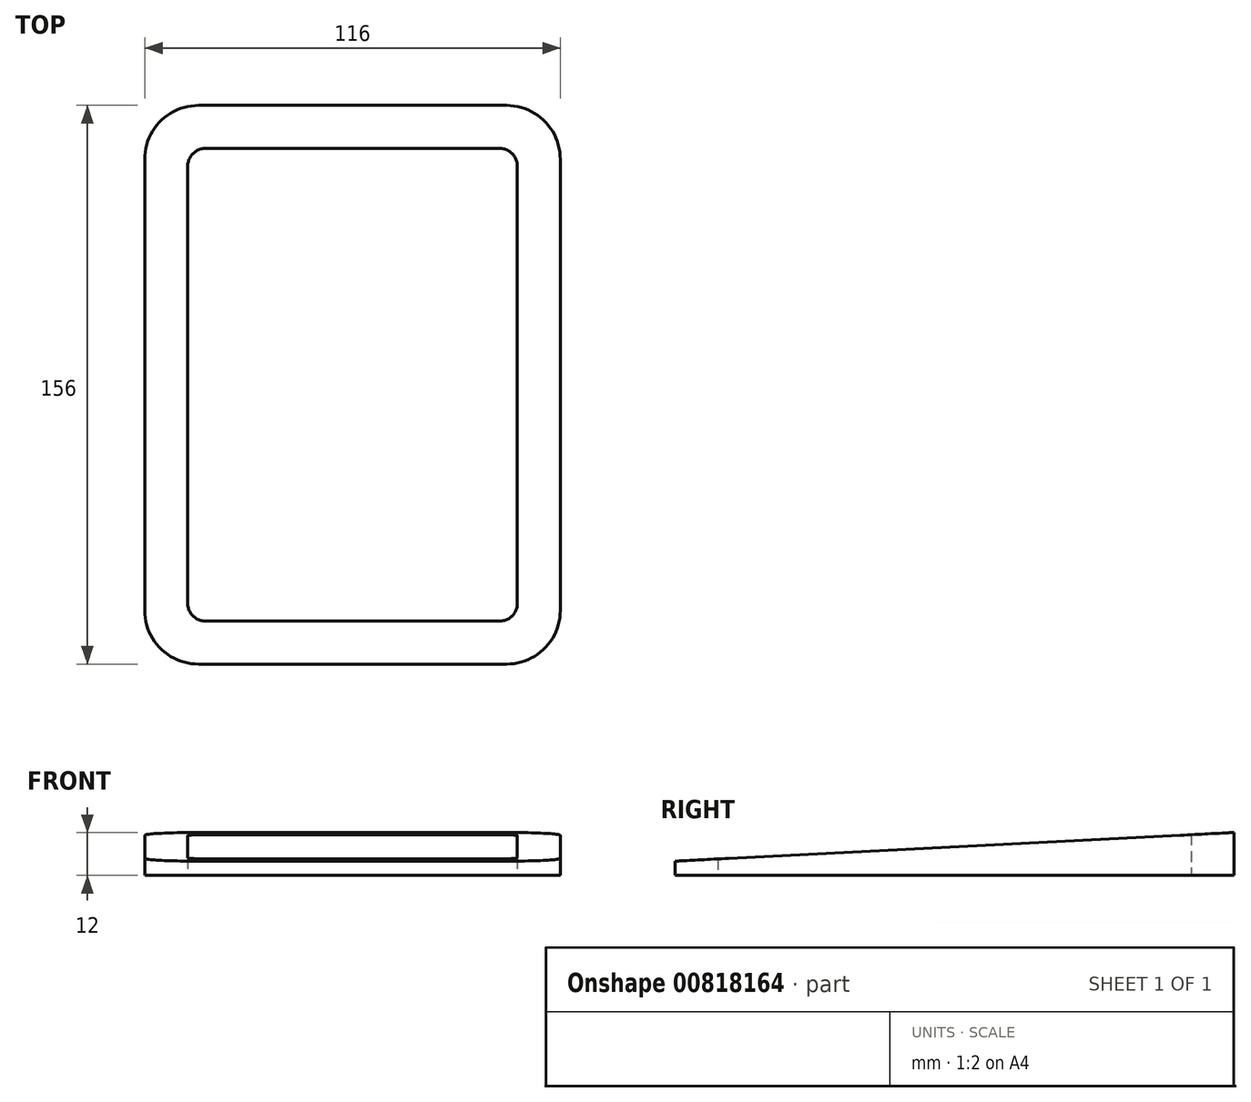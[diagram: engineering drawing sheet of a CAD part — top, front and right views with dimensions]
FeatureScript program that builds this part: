
annotation { "Feature Type Name" : "Feature", "Feature Type Description" : "" }
export const myFeature = defineFeature(function(context is Context, id is Id, definition is map)
    precondition{}
    {
        {
            var Q0;
            Q0=qCreatedBy(makeId("Top.planeOp"),FACE);
            var sketch = newSketch(context, id + "F0", { "sketchPlane" : qUnion([Q0])});
            skLineSegment(sketch, "E0.bottom", {"start": v(-58, 78) * mm, "end": v(58, 78) * mm});
            skLineSegment(sketch, "E0.top", {"start": v(-58, -78) * mm, "end": v(58, -78) * mm});
            skLineSegment(sketch, "E0.left", {"start": v(-58, 78) * mm, "end": v(-58, -78) * mm});
            skLineSegment(sketch, "E0.right", {"start": v(58, 78) * mm, "end": v(58, -78) * mm});
            skLineSegment(sketch, "E1.bottom", {"start": v(-46, 66) * mm, "end": v(46, 66) * mm});
            skLineSegment(sketch, "E1.top", {"start": v(-46, -66) * mm, "end": v(46, -66) * mm});
            skLineSegment(sketch, "E1.left", {"start": v(-46, 66) * mm, "end": v(-46, -66) * mm});
            skLineSegment(sketch, "E1.right", {"start": v(46, 66) * mm, "end": v(46, -66) * mm});
            skSolve(sketch);
        }
        {
            var Q0;
            Q0=makeQuery(id+"F0.imprint","IMPRINT",FACE,{"disambiguationData":[TD([[makeQuery(id+"F0.imprint","IMPRINT",EDGE,{"derivedFrom":sQuery(id+"F0.wireOp",EDGE,"E0.bottom")}),-1.0]])]});
            extrude(context, id + "F1", {"entities" : qUnion([Q0]), "depth" : 12 * mm, "offsetDistance" : 25 * mm});
        }
        {
            var Q0;
            Q0=makeQuery(id+"F1.opExtrude","SWEPT_FACE",FACE,{"disambiguationData":[OSD([sQuery(id+"F0.wireOp",EDGE,"E0.left")])]});
            var sketch = newSketch(context, id + "F2", { "sketchPlane" : qUnion([Q0])});
            skLineSegment(sketch, "E2", {"start": v(78, 4) * mm, "end": v(-78, 12) * mm});
            skLineSegment(sketch, "E3", {"start": v(-78, 12) * mm, "end": v(78, 12) * mm});
            skLineSegment(sketch, "E4", {"start": v(78, 12) * mm, "end": v(78, 4) * mm});
            skSolve(sketch);
        }
        {
            var Q0;
            Q0=makeQuery(id+"F2.imprint","IMPRINT",FACE,{"disambiguationData":[TD([[makeQuery(id+"F2.imprint","IMPRINT",EDGE,{"derivedFrom":sQuery(id+"F2.wireOp",EDGE,"E2")}),-1.0]])]});
            var Q1;
            Q1=makeQuery(id+"F1.opExtrude","SWEPT_FACE",FACE,{"disambiguationData":[OSD([sQuery(id+"F0.wireOp",EDGE,"E0.right")])]});
            extrude(context, id + "F3", {"entities" : qUnion([Q0]), "operationType" : NewBodyOperationType.REMOVE, "endBound" : BoundingType.UP_TO_SURFACE, "oppositeDirection" : true, "depth" : 25 * mm, "endBoundEntityFace" : qUnion([Q1]), "offsetDistance" : 25 * mm});
        }
        {
            var Q0;
            Q0=makeQuery(id+"F1.opExtrude","SWEPT_EDGE",EDGE,{"disambiguationData":[OSD([sQuery(id+"F0.wireOp",EDGE,"E1.bottom"),sQuery(id+"F0.wireOp",EDGE,"E1.right")])]});
            var Q1;
            Q1=makeQuery(id+"F1.opExtrude","SWEPT_EDGE",EDGE,{"disambiguationData":[OSD([sQuery(id+"F0.wireOp",EDGE,"E1.bottom"),sQuery(id+"F0.wireOp",EDGE,"E1.left")])]});
            var Q2;
            Q2=makeQuery(id+"F1.opExtrude","SWEPT_EDGE",EDGE,{"disambiguationData":[OSD([sQuery(id+"F0.wireOp",EDGE,"E1.top"),sQuery(id+"F0.wireOp",EDGE,"E1.left")])]});
            var Q3;
            Q3=makeQuery(id+"F1.opExtrude","SWEPT_EDGE",EDGE,{"disambiguationData":[OSD([sQuery(id+"F0.wireOp",EDGE,"E1.top"),sQuery(id+"F0.wireOp",EDGE,"E1.right")])]});
            fillet(context, id + "F4", {"entities" : qUnion([Q0, Q1, Q2, Q3]), "radius" : 5 * mm, "tangentPropagation" : true, "allowEdgeOverflow" : false});
        }
        {
            var Q0;
            Q0=makeQuery(id+"F1.opExtrude","SWEPT_EDGE",EDGE,{"disambiguationData":[OSD([sQuery(id+"F0.wireOp",EDGE,"E0.top"),sQuery(id+"F0.wireOp",EDGE,"E0.right")])]});
            var Q1;
            Q1=makeQuery(id+"F1.opExtrude","SWEPT_EDGE",EDGE,{"disambiguationData":[OSD([sQuery(id+"F0.wireOp",EDGE,"E0.top"),sQuery(id+"F0.wireOp",EDGE,"E0.left")])]});
            var Q2;
            Q2=makeQuery(id+"F1.opExtrude","SWEPT_EDGE",EDGE,{"disambiguationData":[OSD([sQuery(id+"F0.wireOp",EDGE,"E0.bottom"),sQuery(id+"F0.wireOp",EDGE,"E0.left")])]});
            var Q3;
            Q3=makeQuery(id+"F1.opExtrude","SWEPT_EDGE",EDGE,{"disambiguationData":[OSD([sQuery(id+"F0.wireOp",EDGE,"E0.bottom"),sQuery(id+"F0.wireOp",EDGE,"E0.right")])]});
            fillet(context, id + "F5", {"entities" : qUnion([Q0, Q1, Q2, Q3]), "radius" : 15 * mm, "tangentPropagation" : true, "allowEdgeOverflow" : false});
        }
    });
